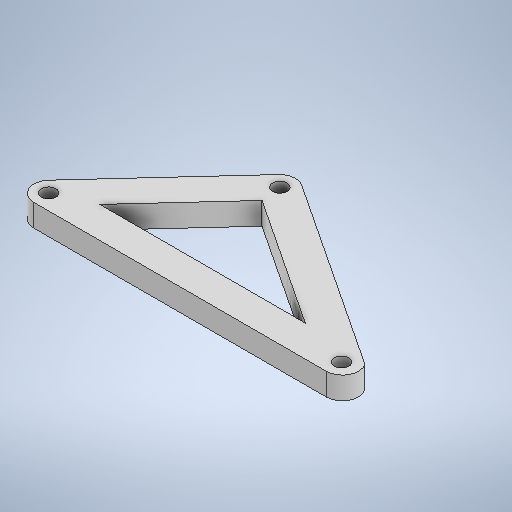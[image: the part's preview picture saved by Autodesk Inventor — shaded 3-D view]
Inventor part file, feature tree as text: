
AUTODESK INVENTOR PART (.ipt)
format: ipt  version: 2025.1 (Build 291241020, 241B)  size: 285,696 bytes
history: native  units: in
note: dims shown in document units (in); Inventor stores cm internally (conversion verified against a paired STEP export)
features: extrude x3, sketch x3, fillet x2
ambient origin geometry x8: Origin, YZ Plane, XZ Plane, XY Plane, X Axis, Y Axis, Z Axis, Center Point
bodies: Solid1 (feature_tree)
feature tree (8):
  extrude  "Extrusion1"  Depth=0.23in
  extrude  "Extrusion2"  Depth=0.1181in
  extrude  "Extrusion3"  Depth=0.2756in
  fillet  "Fillet1"  Radius=0.2756in
  fillet  "Fillet2"  Radius=0.2756in
  sketch  "Sketch1"  dims[d0=2.5866in d2=0.23in]
  sketch  "Sketch2"  dims[d3=0.1181in d4=0.1181in]
  sketch  "Sketch3"  dims[d7=1.563in d8=0.2756in d9=0.2756in d10=0.2756in d11=0.1299in d12=0.1299in d13=0.1299in d14=0.1969in d15=0.0in d16=0.2301in d17=0.1969in d18=0.0in d19=0.3937in d20=0.0in d21=0.1412in d22=0.1412in]
